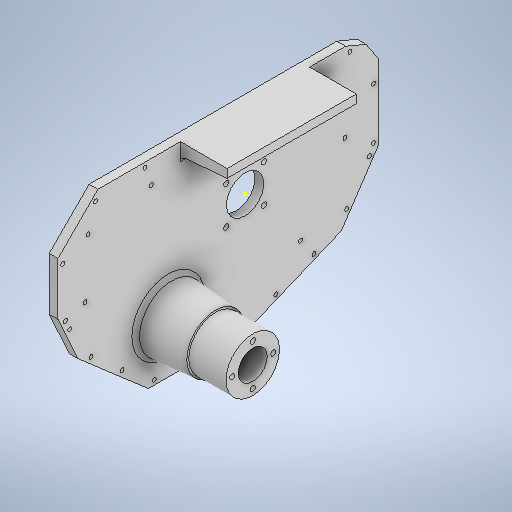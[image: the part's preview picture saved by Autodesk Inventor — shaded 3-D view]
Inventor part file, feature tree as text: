
AUTODESK INVENTOR PART (.ipt)
format: ipt  version: 2025.2 (Build 292293000, 293)  size: 1,307,648 bytes
history: native  units: mm
features: sketch x23, reference x23, projected_geometry x18, extrude x17, chamfer x5, other x5, fillet x2, mirror x1
ambient origin geometry x8: Origin, YZ Plane, XZ Plane, XY Plane, X Axis, Y Axis, Z Axis, Center Point
bodies: Solid1 (feature_tree)
feature tree (94):
  extrude  "Extrusion1"  Depth=76.5mm
  extrude  "Extrusion2"  Depth=4.0mm
  chamfer  "Chamfer1"  Distance=40.0mm Angle=360.0deg
  fillet  "Fillet1"  Radius=7.15585mm
  extrude  "Extrusion3"  Depth=7.1mm TaperAngle=360.0deg
  extrude  "Extrusion4"  Depth=21.7mm TaperAngle=360.0deg
  extrude  "Extrusion5"  Depth=28.0mm
  extrude  "Extrusion6"  Depth=35.5mm TaperAngle=0.0deg
  extrude  "Extrusion7"  Depth=3.0mm TaperAngle=45.0deg
  extrude  "Extrusion8"  Depth=40.1mm
  extrude  "Extrusion9"  TaperAngle=0.0deg  [1 undecoded]
  sketch  "Sketch15"  dims[d62=30.0mm d63=22.0mm]
  chamfer  "Chamfer2"  Distance=40.0mm Angle=360.0deg
  chamfer  "Chamfer3"  [1 undecoded]
  chamfer  "Chamfer4"  Distance=20.5mm
  extrude  "Extrusion11"  Depth=3.0mm
  extrude  "Extrusion12"  Depth=1.5mm
  chamfer  "Chamfer5"  [1 undecoded]
  fillet  "Fillet5"  Radius=4.45mm
  extrude  "Extrusion13"  Depth=22.0mm
  extrude  "Extrusion14"  Depth=6.0mm
  mirror  "Mirror1"
  extrude  "Extrusion15"  Depth=90.0mm
  extrude  "Extrusion16"  Depth=50.0mm
  extrude  "Extrusion17"  Depth=117.0mm
  extrude  "Extrusion18"  Depth=92.0mm
  sketch  "Sketch1"  dims[d0=7.15585mm d1=76.5mm]
  sketch  "Sketch Circular Pattern2"  dims[d2=40.0mm d3=4.0mm]
  sketch  "Sketch Circular Pattern3"  dims[d18=7.1mm d19=40.0mm d21=360.0deg]
  sketch  "Sketch Circular Pattern4"  dims[d28=10.85mm d29=28.0mm]
  sketch  "Sketch2"  dims[d8=45.0deg d9=40.0mm d11=360.0deg d14=7.15585mm]
  sketch  "Sketch3"  dims[d23=21.7mm d24=40.0mm d26=360.0deg]
  sketch  "Sketch4"  dims[d31=6.6mm d32=0.0mm d33=35.5mm d34=0.0mm]
  sketch  "Sketch5"  dims[d35=43.0mm d36=3.0mm d37=35.5mm d38=45.0deg]
  sketch  "Sketch Circular Pattern5"  dims[d39=3.0mm d40=40.1mm]
  sketch  "Sketch6"  dims[d41=28.0mm d42=0.0mm d43=0.0mm d44=0.0mm]
  projected_geometry  "Projected Loop1"
  projected_geometry  "Projected Loop2"
  projected_geometry  "Projected Loop3"
  projected_geometry  "Projected Loop4"
  sketch  "Sketch7"  dims[d52=30.9mm d53=20.5mm d54=0.0mm]
  sketch  "Sketch8"  dims[d55=18.0mm d56=3.0mm]
  sketch  "Sketch13"  dims[d57=6.0mm d58=1.5mm d59=0.0mm d60=0.0mm d61=4.45mm]
  sketch  "Sketch16"  dims[d64=6.0mm d65=0.0mm d66=180.0mm]
  projected_geometry  "Projected Loop5"
  sketch  "Sketch18"  dims[d67=90.0mm d68=92.0mm]
  reference  "Reference3"
  reference  "Reference4"
  reference  "Reference5"
  reference  "Reference6"
  reference  "Reference7"
  reference  "Reference8"
  reference  "Reference9"
  reference  "Reference10"
  reference  "Reference11"
  reference  "Reference12"
  reference  "Reference13"
  reference  "Reference14"
  reference  "Reference15"
  reference  "Reference16"
  reference  "Reference18"
  reference  "Reference19"
  reference  "Reference20"
  reference  "Reference21"
  reference  "Reference22"
  reference  "Reference23"
  reference  "Reference24"
  sketch  "Sketch19"  dims[d85=100.0mm d86=50.0mm]
  reference  "Reference25"
  reference  "Reference26"
  sketch  "Sketch20"  dims[d87=30.0mm d88=117.0mm]
  sketch  "Sketch21"  dims[d89=45.0deg d90=92.0mm]
  sketch  "Sketch22"  dims[d91=45.0mm]
  projected_geometry  "Projected Loop6"
  projected_geometry  "Projected Loop7"
  projected_geometry  "Projected Loop8"
  projected_geometry  "Projected Loop9"
  sketch  "Sketch Circular Pattern6"  dims[d45=4.0mm d46=40.0mm d48=360.0deg d50=0.0mm d51=0.0mm]
  sketch  "Sketch23"  dims[d92=52.0mm]
  projected_geometry  "Projected Loop10"
  projected_geometry  "Projected Loop11"
  projected_geometry  "Projected Loop12"
  sketch  "Sketch24"  dims[d93=10.0mm d94=2.5mm d95=10.0mm d96=0.0mm d104=30.0mm d105=2.0mm d106=45.0deg d107=20.0mm d108=2.0mm d109=45.0deg d110=10.0mm d111=2.0mm d112=45.0deg d113=35.0mm d114=0.0mm d115=92.0mm d116=2.5mm d117=3.3mm d118=0.0mm d119=0.0mm d120=3.0mm d121=35.0mm d122=45.0deg d123=4.0mm d124=3.0mm d125=3.0mm d126=3.0mm d127=3.0mm d128=3.0mm d129=3.0mm d130=0.0mm d131=0.0mm d132=5.6mm d133=5.6mm d134=5.6mm d135=5.6mm d136=5.6mm d137=5.6mm d138=3.0mm d139=0.0mm d140=7.1mm d141=7.1mm d142=7.1mm d143=7.1mm d144=2.0mm d145=0.0mm d146=40.0mm d148=360.0deg d150=0.2mm d151=0.0mm d152=0.2mm d153=0.0mm d154=0.2mm d155=0.0mm]
  projected_geometry  "Projected Loop13"
  projected_geometry  "Projected Loop14"
  projected_geometry  "Projected Loop15"
  projected_geometry  "Projected Loop16"
  projected_geometry  "Projected Loop17"
  projected_geometry  "Projected Loop18"
  parser-record x1  (decoder bookkeeping rows leaked as tree rows — omitted from the tree; the rows remain in map.json)
  other  "WBR.iam"
  other  "inner_body_c:1"
  other  "inner_body_b:1"
  other  "OUT_SHELL:1"
note: 3 required parameter values undecoded (feature->parameter linkage not recoverable at this tier; creation-order binding heuristic only, values carry confidence <= 0.55)
note: 1 file-system path scrubbed to <path> (originals preserved in map.json)
